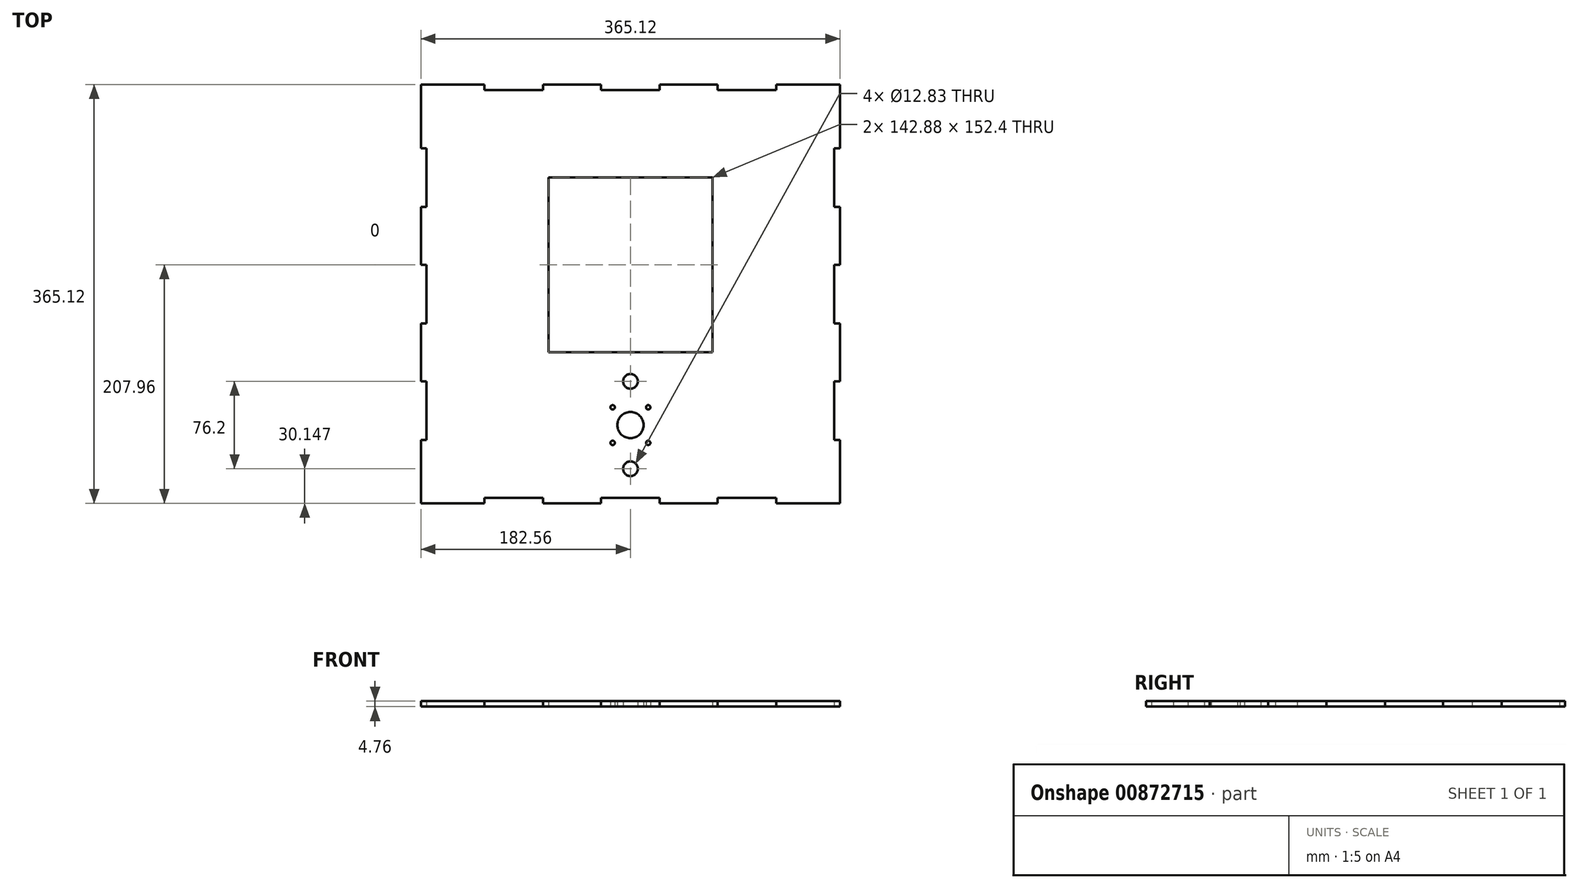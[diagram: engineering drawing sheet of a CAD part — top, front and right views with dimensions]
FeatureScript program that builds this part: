
annotation { "Feature Type Name" : "Feature", "Feature Type Description" : "" }
export const myFeature = defineFeature(function(context is Context, id is Id, definition is map)
    precondition{}
    {
        {
            var Q0;
            Q0=qCreatedBy(makeId("Top.planeOp"),FACE);
            var sketch = newSketch(context, id + "F0", { "sketchPlane" : qUnion([Q0])});
            skLineSegment(sketch, "E0.bottom", {"start": v(182.56, 182.56) * mm, "end": v(-182.56, 182.56) * mm});
            skLineSegment(sketch, "E0.top", {"start": v(182.56, -182.56) * mm, "end": v(-182.56, -182.56) * mm});
            skLineSegment(sketch, "E0.left", {"start": v(182.56, 182.56) * mm, "end": v(182.56, -182.56) * mm});
            skLineSegment(sketch, "E0.right", {"start": v(-182.56, 182.56) * mm, "end": v(-182.56, -182.56) * mm});
            skPoint(sketch, "E0.middle", {"position": v(0, 0) * mm});
            skLineSegment(sketch, "E1.0", {"start": v(177.81, -177.81) * mm, "end": v(-177.81, -177.81) * mm, "construction": true});
            skLineSegment(sketch, "E1.1", {"start": v(177.81, 177.81) * mm, "end": v(177.81, -177.81) * mm, "construction": true});
            skLineSegment(sketch, "E1.2", {"start": v(177.81, 177.81) * mm, "end": v(-177.81, 177.81) * mm, "construction": true});
            skLineSegment(sketch, "E1.3", {"start": v(-177.81, 177.81) * mm, "end": v(-177.81, -177.81) * mm, "construction": true});
            skLineSegment(sketch, "E2.bottom", {"start": v(-182.56, -127.01) * mm, "end": v(-177.8, -127.01) * mm});
            skLineSegment(sketch, "E2.top", {"start": v(-182.56, -76.21) * mm, "end": v(-177.8, -76.21) * mm});
            skLineSegment(sketch, "E2.left", {"start": v(-182.56, -127.01) * mm, "end": v(-182.56, -76.21) * mm});
            skLineSegment(sketch, "E2.right", {"start": v(-177.8, -127.01) * mm, "end": v(-177.8, -76.21) * mm});
            skLineSegment(sketch, "E3.0", {"start": v(-182.69, -127.14) * mm, "end": v(-182.69, -76.09) * mm});
            skLineSegment(sketch, "E3.1", {"start": v(-182.69, -127.14) * mm, "end": v(-177.67, -127.14) * mm});
            skLineSegment(sketch, "E3.2", {"start": v(-177.67, -127.14) * mm, "end": v(-177.67, -76.09) * mm});
            skLineSegment(sketch, "E3.3", {"start": v(-182.69, -76.09) * mm, "end": v(-177.67, -76.09) * mm});
            skLineSegment(sketch, "E4", {"start": v(0, 182.56) * mm, "end": v(0, -182.56) * mm, "construction": true});
            skLineSegment(sketch, "E5", {"start": v(182.56, 0) * mm, "end": v(-182.69, 0) * mm, "construction": true});
            skLineSegment(sketch, "E6.bottom", {"start": v(-127.01, -177.81) * mm, "end": v(-76.21, -177.81) * mm});
            skLineSegment(sketch, "E6.top", {"start": v(-127.01, -182.58) * mm, "end": v(-76.21, -182.58) * mm});
            skLineSegment(sketch, "E6.left", {"start": v(-127.01, -177.81) * mm, "end": v(-127.01, -182.58) * mm});
            skLineSegment(sketch, "E6.right", {"start": v(-76.21, -177.81) * mm, "end": v(-76.21, -182.58) * mm});
            skLineSegment(sketch, "E7.0", {"start": v(-127.14, -177.69) * mm, "end": v(-76.09, -177.69) * mm});
            skLineSegment(sketch, "E7.1", {"start": v(-127.14, -177.69) * mm, "end": v(-127.14, -182.7) * mm});
            skLineSegment(sketch, "E7.2", {"start": v(-127.14, -182.7) * mm, "end": v(-76.09, -182.7) * mm});
            skLineSegment(sketch, "E7.3", {"start": v(-76.09, -177.69) * mm, "end": v(-76.09, -182.7) * mm});
            skLineSegment(sketch, "E8.0.1.0", {"start": v(-177.67, -25.54) * mm, "end": v(-177.67, 25.51) * mm});
            skLineSegment(sketch, "E8.0.1.1", {"start": v(-177.8, -25.41) * mm, "end": v(-177.8, 25.39) * mm});
            skLineSegment(sketch, "E8.0.1.2", {"start": v(-182.69, -25.54) * mm, "end": v(-182.69, 25.51) * mm});
            skLineSegment(sketch, "E8.0.1.3", {"start": v(-182.56, -25.41) * mm, "end": v(-182.56, 25.39) * mm});
            skLineSegment(sketch, "E8.0.1.4", {"start": v(-182.56, 25.39) * mm, "end": v(-177.8, 25.39) * mm});
            skLineSegment(sketch, "E8.0.1.5", {"start": v(-182.69, 25.51) * mm, "end": v(-177.67, 25.51) * mm});
            skLineSegment(sketch, "E8.0.1.6", {"start": v(-182.69, -25.54) * mm, "end": v(-177.67, -25.54) * mm});
            skLineSegment(sketch, "E8.0.1.7", {"start": v(-182.56, -25.41) * mm, "end": v(-177.8, -25.41) * mm});
            skLineSegment(sketch, "E8.0.2.0", {"start": v(-177.67, 76.06) * mm, "end": v(-177.67, 127.11) * mm});
            skLineSegment(sketch, "E8.0.2.1", {"start": v(-177.8, 76.19) * mm, "end": v(-177.8, 126.99) * mm});
            skLineSegment(sketch, "E8.0.2.2", {"start": v(-182.69, 76.06) * mm, "end": v(-182.69, 127.11) * mm});
            skLineSegment(sketch, "E8.0.2.3", {"start": v(-182.56, 76.19) * mm, "end": v(-182.56, 126.99) * mm});
            skLineSegment(sketch, "E8.0.2.4", {"start": v(-182.56, 126.99) * mm, "end": v(-177.8, 126.99) * mm});
            skLineSegment(sketch, "E8.0.2.5", {"start": v(-182.69, 127.11) * mm, "end": v(-177.67, 127.11) * mm});
            skLineSegment(sketch, "E8.0.2.6", {"start": v(-182.69, 76.06) * mm, "end": v(-177.67, 76.06) * mm});
            skLineSegment(sketch, "E8.0.2.7", {"start": v(-182.56, 76.19) * mm, "end": v(-177.8, 76.19) * mm});
            skLineSegment(sketch, "E8.direction1", {"start": v(-182.56, -127.01) * mm, "end": v(-157.16, -127.01) * mm, "construction": true});
            skLineSegment(sketch, "E8.direction2", {"start": v(-182.56, -127.01) * mm, "end": v(-182.56, -25.41) * mm, "construction": true});
            skLineSegment(sketch, "E9.1.0.0", {"start": v(-25.54, -177.69) * mm, "end": v(-25.54, -182.7) * mm});
            skLineSegment(sketch, "E9.1.0.1", {"start": v(25.39, -177.81) * mm, "end": v(25.39, -182.58) * mm});
            skLineSegment(sketch, "E9.1.0.2", {"start": v(-25.41, -177.81) * mm, "end": v(-25.41, -182.58) * mm});
            skLineSegment(sketch, "E9.1.0.3", {"start": v(-25.41, -182.58) * mm, "end": v(25.39, -182.58) * mm});
            skLineSegment(sketch, "E9.1.0.4", {"start": v(-25.41, -177.81) * mm, "end": v(25.39, -177.81) * mm});
            skLineSegment(sketch, "E9.1.0.5", {"start": v(25.51, -177.69) * mm, "end": v(25.51, -182.7) * mm});
            skLineSegment(sketch, "E9.1.0.6", {"start": v(-25.54, -182.7) * mm, "end": v(25.51, -182.7) * mm});
            skLineSegment(sketch, "E9.1.0.7", {"start": v(-25.54, -177.69) * mm, "end": v(25.51, -177.69) * mm});
            skLineSegment(sketch, "E9.2.0.0", {"start": v(76.06, -177.69) * mm, "end": v(76.06, -182.7) * mm});
            skLineSegment(sketch, "E9.2.0.1", {"start": v(126.99, -177.81) * mm, "end": v(126.99, -182.58) * mm});
            skLineSegment(sketch, "E9.2.0.2", {"start": v(76.19, -177.81) * mm, "end": v(76.19, -182.58) * mm});
            skLineSegment(sketch, "E9.2.0.3", {"start": v(76.19, -182.58) * mm, "end": v(126.99, -182.58) * mm});
            skLineSegment(sketch, "E9.2.0.4", {"start": v(76.19, -177.81) * mm, "end": v(126.99, -177.81) * mm});
            skLineSegment(sketch, "E9.2.0.5", {"start": v(127.11, -177.69) * mm, "end": v(127.11, -182.7) * mm});
            skLineSegment(sketch, "E9.2.0.6", {"start": v(76.06, -182.7) * mm, "end": v(127.11, -182.7) * mm});
            skLineSegment(sketch, "E9.2.0.7", {"start": v(76.06, -177.69) * mm, "end": v(127.11, -177.69) * mm});
            skLineSegment(sketch, "E9.direction1", {"start": v(-127.01, -182.58) * mm, "end": v(-25.41, -182.58) * mm, "construction": true});
            skLineSegment(sketch, "E10.MirrorCS", {"start": v(-127.14, 177.69) * mm, "end": v(-127.14, 182.7) * mm});
            skLineSegment(sketch, "E11.MirrorCS", {"start": v(-25.54, 177.69) * mm, "end": v(-25.54, 182.7) * mm});
            skLineSegment(sketch, "E12.MirrorCS", {"start": v(-127.01, 177.81) * mm, "end": v(-127.01, 182.58) * mm});
            skLineSegment(sketch, "E13.MirrorCS", {"start": v(-25.41, 177.81) * mm, "end": v(-25.41, 182.58) * mm});
            skLineSegment(sketch, "E14.MirrorCS", {"start": v(-76.09, 177.69) * mm, "end": v(-76.09, 182.7) * mm});
            skLineSegment(sketch, "E15.MirrorCS", {"start": v(127.11, 177.69) * mm, "end": v(127.11, 182.7) * mm});
            skLineSegment(sketch, "E16.MirrorCS", {"start": v(76.19, 177.81) * mm, "end": v(76.19, 182.58) * mm});
            skLineSegment(sketch, "E17.MirrorCS", {"start": v(25.39, 177.81) * mm, "end": v(25.39, 182.58) * mm});
            skLineSegment(sketch, "E18.MirrorCS", {"start": v(25.51, 177.69) * mm, "end": v(25.51, 182.7) * mm});
            skLineSegment(sketch, "E19.MirrorCS", {"start": v(126.99, 177.81) * mm, "end": v(126.99, 182.58) * mm});
            skLineSegment(sketch, "E20.MirrorCS", {"start": v(76.06, 177.69) * mm, "end": v(76.06, 182.7) * mm});
            skLineSegment(sketch, "E21.MirrorCS", {"start": v(-76.21, 177.81) * mm, "end": v(-76.21, 182.58) * mm});
            skLineSegment(sketch, "E22.MirrorCS", {"start": v(-25.41, 182.58) * mm, "end": v(25.39, 182.58) * mm});
            skLineSegment(sketch, "E23.MirrorCS", {"start": v(-25.54, 177.69) * mm, "end": v(25.51, 177.69) * mm});
            skLineSegment(sketch, "E24.MirrorCS", {"start": v(-25.41, 177.81) * mm, "end": v(25.39, 177.81) * mm});
            skLineSegment(sketch, "E25.MirrorCS", {"start": v(-25.54, 182.7) * mm, "end": v(25.51, 182.7) * mm});
            skLineSegment(sketch, "E26.MirrorCS", {"start": v(76.06, 177.69) * mm, "end": v(127.11, 177.69) * mm});
            skLineSegment(sketch, "E27.MirrorCS", {"start": v(-127.14, 177.69) * mm, "end": v(-76.09, 177.69) * mm});
            skLineSegment(sketch, "E28.MirrorCS", {"start": v(-127.14, 182.7) * mm, "end": v(-76.09, 182.7) * mm});
            skLineSegment(sketch, "E29.MirrorCS", {"start": v(-127.01, 177.81) * mm, "end": v(-76.21, 177.81) * mm});
            skLineSegment(sketch, "E30.MirrorCS", {"start": v(-127.01, 182.58) * mm, "end": v(-76.21, 182.58) * mm});
            skLineSegment(sketch, "E31.MirrorCS", {"start": v(76.19, 177.81) * mm, "end": v(126.99, 177.81) * mm});
            skLineSegment(sketch, "E32.MirrorCS", {"start": v(76.06, 182.7) * mm, "end": v(127.11, 182.7) * mm});
            skLineSegment(sketch, "E33.MirrorCS", {"start": v(76.19, 182.58) * mm, "end": v(126.99, 182.58) * mm});
            skLineSegment(sketch, "E34.MirrorCS", {"start": v(-127.01, 182.58) * mm, "end": v(-25.41, 182.58) * mm, "construction": true});
            skLineSegment(sketch, "E35.MirrorCS", {"start": v(182.56, -127.01) * mm, "end": v(177.8, -127.01) * mm});
            skLineSegment(sketch, "E36.MirrorCS", {"start": v(182.69, -127.14) * mm, "end": v(177.67, -127.14) * mm});
            skLineSegment(sketch, "E37.MirrorCS", {"start": v(182.56, -25.41) * mm, "end": v(177.8, -25.41) * mm});
            skLineSegment(sketch, "E38.MirrorCS", {"start": v(182.56, -76.21) * mm, "end": v(177.8, -76.21) * mm});
            skLineSegment(sketch, "E39.MirrorCS", {"start": v(182.69, -76.09) * mm, "end": v(177.67, -76.09) * mm});
            skLineSegment(sketch, "E40.MirrorCS", {"start": v(182.69, -25.54) * mm, "end": v(177.67, -25.54) * mm});
            skLineSegment(sketch, "E41.MirrorCS", {"start": v(182.69, 127.11) * mm, "end": v(177.67, 127.11) * mm});
            skLineSegment(sketch, "E42.MirrorCS", {"start": v(182.56, 25.39) * mm, "end": v(177.8, 25.39) * mm});
            skLineSegment(sketch, "E43.MirrorCS", {"start": v(182.56, 76.19) * mm, "end": v(177.8, 76.19) * mm});
            skLineSegment(sketch, "E44.MirrorCS", {"start": v(182.69, 76.06) * mm, "end": v(177.67, 76.06) * mm});
            skLineSegment(sketch, "E45.MirrorCS", {"start": v(182.56, 126.99) * mm, "end": v(177.8, 126.99) * mm});
            skLineSegment(sketch, "E46.MirrorCS", {"start": v(182.69, 25.51) * mm, "end": v(177.67, 25.51) * mm});
            skLineSegment(sketch, "E47.MirrorCS", {"start": v(177.8, -127.01) * mm, "end": v(177.8, -76.21) * mm});
            skLineSegment(sketch, "E48.MirrorCS", {"start": v(182.56, -127.01) * mm, "end": v(182.56, -76.21) * mm});
            skLineSegment(sketch, "E49.MirrorCS", {"start": v(177.8, 76.19) * mm, "end": v(177.8, 126.99) * mm});
            skLineSegment(sketch, "E50.MirrorCS", {"start": v(177.8, -25.41) * mm, "end": v(177.8, 25.39) * mm});
            skLineSegment(sketch, "E51.MirrorCS", {"start": v(182.69, -25.54) * mm, "end": v(182.69, 25.51) * mm});
            skLineSegment(sketch, "E52.MirrorCS", {"start": v(177.67, -127.14) * mm, "end": v(177.67, -76.09) * mm});
            skLineSegment(sketch, "E53.MirrorCS", {"start": v(182.69, -127.14) * mm, "end": v(182.69, -76.09) * mm});
            skLineSegment(sketch, "E54.MirrorCS", {"start": v(177.67, 76.06) * mm, "end": v(177.67, 127.11) * mm});
            skLineSegment(sketch, "E55.MirrorCS", {"start": v(177.67, -25.54) * mm, "end": v(177.67, 25.51) * mm});
            skLineSegment(sketch, "E56.MirrorCS", {"start": v(182.56, 76.19) * mm, "end": v(182.56, 126.99) * mm});
            skLineSegment(sketch, "E57.MirrorCS", {"start": v(182.56, -25.41) * mm, "end": v(182.56, 25.39) * mm});
            skLineSegment(sketch, "E58.MirrorCS", {"start": v(182.69, 76.06) * mm, "end": v(182.69, 127.11) * mm});
            skLineSegment(sketch, "E59.MirrorCS", {"start": v(182.56, -127.01) * mm, "end": v(182.56, -25.41) * mm, "construction": true});
            skLineSegment(sketch, "E60.bottom", {"start": v(-71.44, -63.5) * mm, "end": v(71.44, -63.5) * mm});
            skLineSegment(sketch, "E60.top", {"start": v(-71.44, 63.5) * mm, "end": v(71.44, 63.5) * mm});
            skLineSegment(sketch, "E60.left", {"start": v(-71.44, -63.5) * mm, "end": v(-71.44, 63.5) * mm});
            skLineSegment(sketch, "E60.right", {"start": v(71.44, -63.5) * mm, "end": v(71.44, 63.5) * mm});
            skLineSegment(sketch, "E61.top", {"start": v(-71.44, -88.9) * mm, "end": v(71.44, -88.9) * mm});
            skLineSegment(sketch, "E61.left", {"start": v(-71.44, -63.5) * mm, "end": v(-71.44, -88.9) * mm});
            skLineSegment(sketch, "E61.right", {"start": v(71.44, -63.5) * mm, "end": v(71.44, -88.9) * mm});
            skCircle(sketch, "E62", {"center": v(0, 139.71) * mm, "radius": 11.43 * mm});
            skCircle(sketch, "E63", {"center": v(15.5, 155.2) * mm, "radius": 1.9 * mm});
            skCircle(sketch, "E64.1.0", {"center": v(-15.5, 155.2) * mm, "radius": 1.9 * mm});
            skCircle(sketch, "E64.2.0", {"center": v(-15.5, 124.22) * mm, "radius": 1.9 * mm});
            skCircle(sketch, "E64.3.0", {"center": v(15.5, 124.22) * mm, "radius": 1.9 * mm});
            skCircle(sketch, "E65", {"center": v(0, -114.31) * mm, "radius": 11.43 * mm});
            skCircle(sketch, "E66", {"center": v(15.5, -98.82) * mm, "radius": 1.9 * mm});
            skCircle(sketch, "E67.1.0", {"center": v(-15.5, -98.82) * mm, "radius": 1.9 * mm});
            skCircle(sketch, "E67.2.0", {"center": v(-15.5, -129.8) * mm, "radius": 1.9 * mm});
            skCircle(sketch, "E67.3.0", {"center": v(15.5, -129.8) * mm, "radius": 1.9 * mm});
            skCircle(sketch, "E68", {"center": v(0, -152.41) * mm, "radius": 6.41 * mm});
            skLineSegment(sketch, "E69", {"start": v(-57.51, -114.31) * mm, "end": v(55.13, -114.31) * mm, "construction": true});
            skCircle(sketch, "E70.MirrorC", {"center": v(0, -76.21) * mm, "radius": 6.41 * mm});
            skLineSegment(sketch, "E71.0", {"start": v(-71.44, 101.6) * mm, "end": v(71.44, 101.6) * mm});
            skLineSegment(sketch, "E72", {"start": v(-71.44, 101.6) * mm, "end": v(-71.44, 63.5) * mm});
            skLineSegment(sketch, "E73", {"start": v(71.44, 101.6) * mm, "end": v(71.44, 63.5) * mm});
            skLineSegment(sketch, "E74", {"start": v(-71.44, -50.8) * mm, "end": v(71.44, -50.8) * mm});
            skSolve(sketch);
        }
        {
            var Q0;
            {var subQ5=sQuery(id+"F0.wireOp",EDGE,"E3.2");Q0=makeQuery(id+"F0.imprint","IMPRINT",FACE,{"disambiguationData":[TD([[makeQuery(id+"F0.imprint","IMPRINT",EDGE,{"derivedFrom":subQ5}),-1.0]])]});}
            var Q1;
            Q1=makeQuery(id+"F0.imprint","IMPRINT",FACE,{"disambiguationData":[TD([[makeQuery(id+"F0.imprint","IMPRINT",EDGE,{"derivedFrom":sQuery(id+"F0.wireOp",EDGE,"E64.2.0")}),1.0]])]});
            var Q2;
            Q2=makeQuery(id+"F0.imprint","IMPRINT",FACE,{"disambiguationData":[TD([[makeQuery(id+"F0.imprint","IMPRINT",EDGE,{"derivedFrom":sQuery(id+"F0.wireOp",EDGE,"E64.3.0")}),1.0]])]});
            var Q3;
            Q3=makeQuery(id+"F0.imprint","IMPRINT",FACE,{"disambiguationData":[TD([[makeQuery(id+"F0.imprint","IMPRINT",EDGE,{"derivedFrom":sQuery(id+"F0.wireOp",EDGE,"E63")}),1.0]])]});
            var Q4;
            Q4=makeQuery(id+"F0.imprint","IMPRINT",FACE,{"disambiguationData":[TD([[makeQuery(id+"F0.imprint","IMPRINT",EDGE,{"derivedFrom":sQuery(id+"F0.wireOp",EDGE,"E64.1.0")}),1.0]])]});
            var Q5;
            Q5=makeQuery(id+"F0.imprint","IMPRINT",FACE,{"disambiguationData":[TD([[makeQuery(id+"F0.imprint","IMPRINT",EDGE,{"derivedFrom":sQuery(id+"F0.wireOp",EDGE,"E62")}),1.0]])]});
            var Q6;
            Q6=makeQuery(id+"F0.imprint","IMPRINT",FACE,{"disambiguationData":[TD([[makeQuery(id+"F0.imprint","IMPRINT",EDGE,{"derivedFrom":sQuery(id+"F0.wireOp",EDGE,"E60.bottom")}),-1.0]])]});
            var Q7;
            {var subQ0=sQuery(id+"F0.wireOp",EDGE,"E60.bottom");Q7=makeQuery(id+"F0.imprint","IMPRINT",FACE,{"disambiguationData":[TD([[makeQuery(id+"F0.imprint","IMPRINT",EDGE,{"derivedFrom":subQ0}),1.0]])]});}
            extrude(context, id + "F1", {"entities" : qUnion([Q0, Q1, Q2, Q3, Q4, Q5, Q6, Q7]), "depth" : 4.76 * mm, "offsetDistance" : 25.4 * mm});
        }
    });
